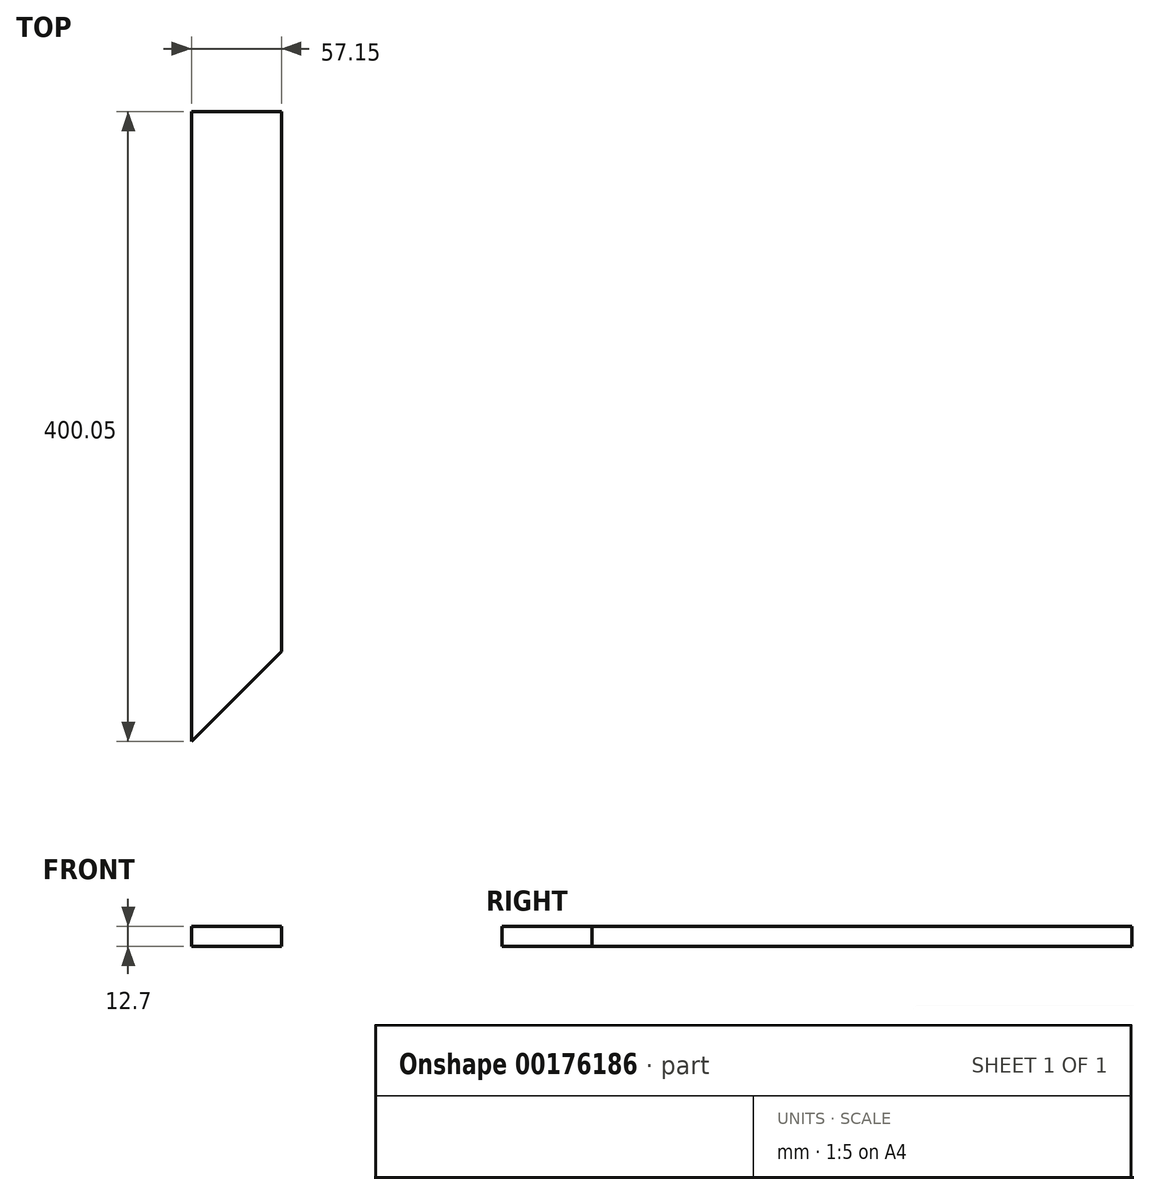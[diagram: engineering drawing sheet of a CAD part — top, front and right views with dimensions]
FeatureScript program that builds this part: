
annotation { "Feature Type Name" : "Feature", "Feature Type Description" : "" }
export const myFeature = defineFeature(function(context is Context, id is Id, definition is map)
    precondition{}
    {
        {
            var Q0;
            Q0=qCreatedBy(makeId("Top.planeOp"),FACE);
            var sketch = newSketch(context, id + "F0", { "sketchPlane" : qUnion([Q0])});
            skLineSegment(sketch, "E0.top", {"start": v(0, 400.05) * mm, "end": v(57.15, 400.05) * mm});
            skLineSegment(sketch, "E0.left", {"start": v(0, 0) * mm, "end": v(0, 400.05) * mm});
            skLineSegment(sketch, "E0.right", {"start": v(57.15, 57.15) * mm, "end": v(57.15, 400.05) * mm});
            skLineSegment(sketch, "E1", {"start": v(0, 0) * mm, "end": v(57.15, 57.15) * mm});
            skSolve(sketch);
        }
        {
            var Q0;
            Q0=makeQuery(id+"F0.imprint","IMPRINT",FACE,{"disambiguationData":[TD([[makeQuery(id+"F0.imprint","IMPRINT",EDGE,{"derivedFrom":sQuery(id+"F0.wireOp",EDGE,"E0.top")}),-1.0]])]});
            extrude(context, id + "F1", {"entities" : qUnion([Q0]), "depth" : 12.7 * mm});
        }
    });
